# Revit family: Faucet-Spray_Kit-KOHLER-LUXE-K-77364X_1
name_source: partatom
category: Plumbing Fixtures
revit_build: Autodesk Revit 2017 (Build: 20160225_1515(x64)
units: mm (PartAtom-declared; Revit-internal decimal feet)

## family parameters
Cut with Voids When Loaded = No
Host = Face
OmniClass Number = 23.31.11.00
OmniClass Title = Faucets
Part Type = Normal
Room Calculation Point = No
Round Connector Dimension = Use Diameter
Shared = No

## types (2) — shared parameters
ADA Compliant = No
Assembly Code = D2010
CW Connection = Yes
Cold Water Inlet = Cold Water Inlet
Date Modified = 12/18/2020
Default Elevation = 36"
Drain Included = No
Faucet Hole Spacing = 0"
Finish = Kohler-Metal-CP-Polished_Chrome
Flow Rate = 3 GPM
HW Connection = No
Handle Clearance = 1 3/4"
Height = 7 11/16"
Hot Water Inlet = Hot Water Inlet
Length = 2 3/4"
Manufacturer = KOHLER Co.
Master Format 2014 = 22 41 39
Master Format 2014 Name = Residential Faucets, Supplies, and Trim
Material = Premium Metal Construction
Pressure = 87.02 psi
Product Name = LUXE
Spout Reach = 0"
URL = https://www.kohler.co.th
Vent Connection = No
Waste Connection = No
Waste Water Outlet = Waste Water Outlet
WaterSense Certified = No
Width = 1 13/16"

## per-type parameters (varying)
| type | A | Connector Angle | Connector Dist | Description | Model | Product Documentation Link | Product Page URL | Type | With Handle | Without Handle |
| Without Handle, CP-Polished Chrome | 5/8" | 90.00° | 0" | Toilet sprayer with flexible hose and hanging hook | K-77364X-CP | http://resources.kohler.com | https://www.kohler.co.th | 1 | No | Yes |
| With Handle, CP-Polished Chrome | 0" | 0.00° | 1 1/8" | HYGIENE SPRAY W/ ANGLE STOP | K-77364X-AS-CP |  |  | 2 | Yes | No |

## geometry (parser evidence)
native form markers: Sweep x3
no freeform markers — native parametric forms only
